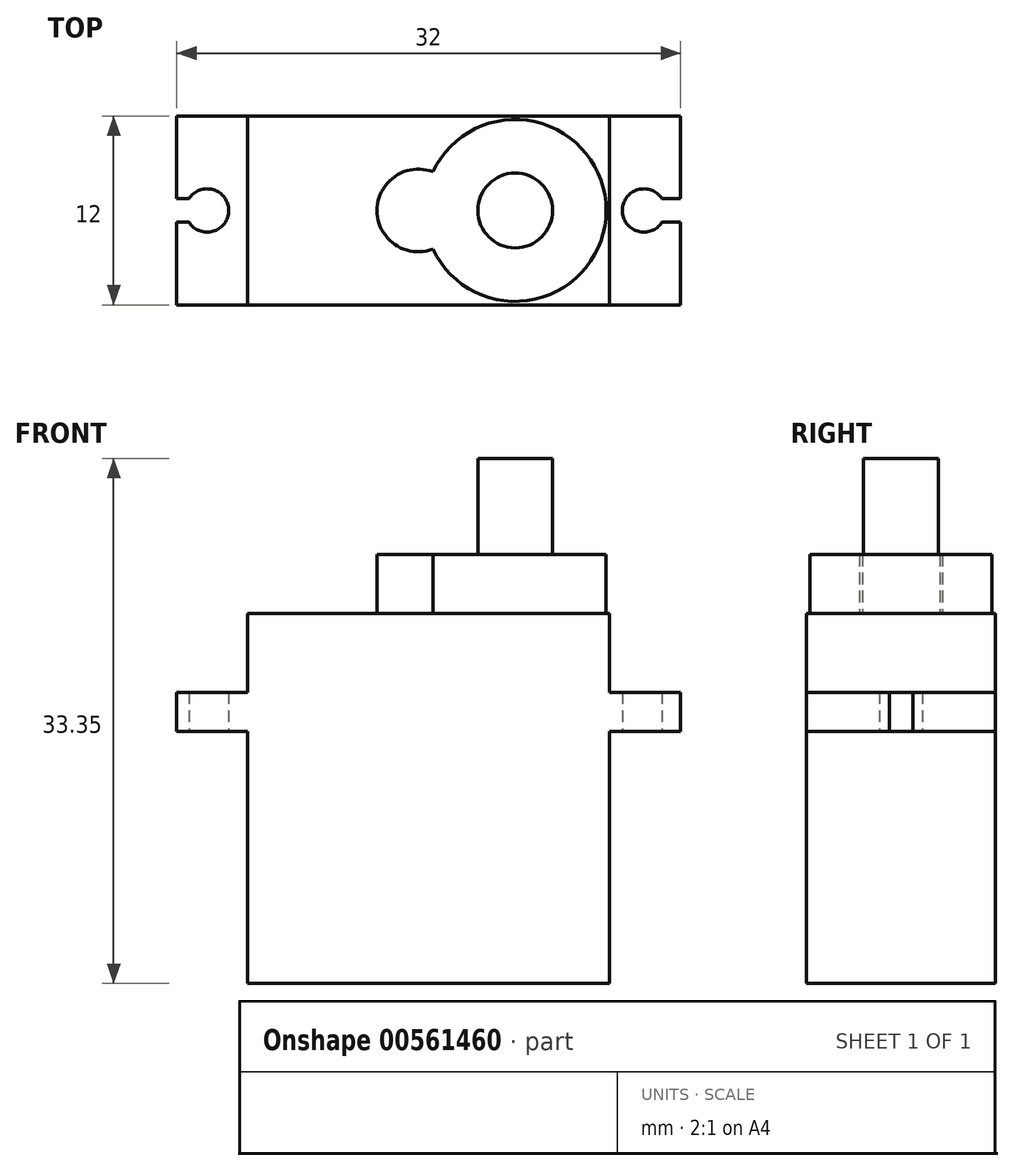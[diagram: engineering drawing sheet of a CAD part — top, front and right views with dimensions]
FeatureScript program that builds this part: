
annotation { "Feature Type Name" : "Feature", "Feature Type Description" : "" }
export const myFeature = defineFeature(function(context is Context, id is Id, definition is map)
    precondition{}
    {
        {
            var Q0;
            Q0=qCreatedBy(makeId("Top.planeOp"),FACE);
            var sketch = newSketch(context, id + "F0", { "sketchPlane" : qUnion([Q0])});
            skLineSegment(sketch, "E0.bottom", {"start": v(-11.3, 6) * mm, "end": v(11.7, 6) * mm});
            skLineSegment(sketch, "E0.top", {"start": v(-11.3, -6) * mm, "end": v(11.7, -6) * mm});
            skLineSegment(sketch, "E0.left", {"start": v(-11.3, 6) * mm, "end": v(-11.3, -6) * mm});
            skLineSegment(sketch, "E0.right", {"start": v(11.7, 6) * mm, "end": v(11.7, -6) * mm});
            skLineSegment(sketch, "E1.bottom", {"start": v(16.2, -6) * mm, "end": v(-15.8, -6) * mm});
            skLineSegment(sketch, "E1.top", {"start": v(16.2, 6) * mm, "end": v(-15.8, 6) * mm});
            skLineSegment(sketch, "E1.left", {"start": v(16.2, -6) * mm, "end": v(16.2, 6) * mm});
            skLineSegment(sketch, "E1.right", {"start": v(-15.8, -6) * mm, "end": v(-15.8, 6) * mm});
            skCircle(sketch, "E2", {"center": v(13.88, 0) * mm, "radius": 1.38 * mm});
            skPoint(sketch, "E2.centerSnap0", {"position": v(11.7, 0) * mm});
            skCircle(sketch, "E3", {"center": v(-13.88, 0) * mm, "radius": 1.38 * mm});
            skLineSegment(sketch, "E4.bottom", {"start": v(-29.2, 0.75) * mm, "end": v(30.8, 0.75) * mm});
            skLineSegment(sketch, "E4.top", {"start": v(-29.2, -0.75) * mm, "end": v(30.8, -0.75) * mm});
            skLineSegment(sketch, "E4.left", {"start": v(-29.2, 0.75) * mm, "end": v(-29.2, -0.75) * mm});
            skLineSegment(sketch, "E4.right", {"start": v(30.8, 0.75) * mm, "end": v(30.8, -0.75) * mm});
            skCircle(sketch, "E5", {"center": v(5.7, 0) * mm, "radius": 5.78 * mm});
            skCircle(sketch, "E6", {"center": v(-0.45, 0) * mm, "radius": 2.62 * mm});
            skSolve(sketch);
        }
        {
            var Q0;
            {var subQ0=sQuery(id+"F0.wireOp",EDGE,"E1.top");var subQ1=sQuery(id+"F0.wireOp",EDGE,"E0.left");var subQ2=makeQuery(id+"F0.imprint","INTERSECT",VERTEX,{"derivedFrom":[subQ1,subQ0]});Q0=makeQuery(id+"F0.imprint","IMPRINT",FACE,{"disambiguationData":[TD([[makeQuery(id+"F0.imprint","IMPRINT",EDGE,{"disambiguationData":[TD([[subQ2,-1.0]])],"derivedFrom":subQ1}),1.0]])]});}
            var Q1;
            {var subQ0=sQuery(id+"F0.wireOp",EDGE,"E1.bottom");var subQ1=sQuery(id+"F0.wireOp",EDGE,"E0.left");var subQ2=makeQuery(id+"F0.imprint","INTERSECT",VERTEX,{"derivedFrom":[subQ1,subQ0]});Q1=makeQuery(id+"F0.imprint","IMPRINT",FACE,{"disambiguationData":[TD([[makeQuery(id+"F0.imprint","IMPRINT",EDGE,{"disambiguationData":[TD([[subQ2,1.0]])],"derivedFrom":subQ1}),1.0]])]});}
            var Q2;
            {var subQ0=sQuery(id+"F0.wireOp",EDGE,"E4.bottom");var subQ1=sQuery(id+"F0.wireOp",EDGE,"E0.left");var subQ2=makeQuery(id+"F0.imprint","INTERSECT",VERTEX,{"derivedFrom":[subQ1,subQ0]});Q2=makeQuery(id+"F0.imprint","IMPRINT",FACE,{"disambiguationData":[TD([[makeQuery(id+"F0.imprint","IMPRINT",EDGE,{"disambiguationData":[TD([[subQ2,-1.0]])],"derivedFrom":subQ1}),1.0]])]});}
            var Q3;
            {var subQ0=sQuery(id+"F0.wireOp",EDGE,"E4.bottom");var subQ1=sQuery(id+"F0.wireOp",EDGE,"E0.left");var subQ2=makeQuery(id+"F0.imprint","INTERSECT",VERTEX,{"derivedFrom":[subQ1,subQ0]});Q3=makeQuery(id+"F0.imprint","IMPRINT",FACE,{"disambiguationData":[TD([[makeQuery(id+"F0.imprint","IMPRINT",EDGE,{"disambiguationData":[TD([[subQ2,-1.0]])],"derivedFrom":subQ1}),-1.0]])]});}
            var Q4;
            {var subQ4=sQuery(id+"F0.wireOp",EDGE,"E1.top");var subQ5=sQuery(id+"F0.wireOp",EDGE,"E0.left");var subQ6=makeQuery(id+"F0.imprint","INTERSECT",VERTEX,{"derivedFrom":[subQ5,subQ4]});Q4=makeQuery(id+"F0.imprint","IMPRINT",FACE,{"disambiguationData":[TD([[makeQuery(id+"F0.imprint","IMPRINT",EDGE,{"disambiguationData":[TD([[subQ6,-1.0]])],"derivedFrom":subQ5}),-1.0]])]});}
            var Q5;
            {var subQ4=sQuery(id+"F0.wireOp",EDGE,"E1.bottom");var subQ5=sQuery(id+"F0.wireOp",EDGE,"E0.left");var subQ6=makeQuery(id+"F0.imprint","INTERSECT",VERTEX,{"derivedFrom":[subQ5,subQ4]});Q5=makeQuery(id+"F0.imprint","IMPRINT",FACE,{"disambiguationData":[TD([[makeQuery(id+"F0.imprint","IMPRINT",EDGE,{"disambiguationData":[TD([[subQ6,1.0]])],"derivedFrom":subQ5}),-1.0]])]});}
            var Q6;
            {var subQ1=sQuery(id+"F0.wireOp",EDGE,"E1.top");var subQ5=sQuery(id+"F0.wireOp",EDGE,"E0.right");var subQ6=makeQuery(id+"F0.imprint","INTERSECT",VERTEX,{"derivedFrom":[subQ5,subQ1]});Q6=makeQuery(id+"F0.imprint","IMPRINT",FACE,{"disambiguationData":[TD([[makeQuery(id+"F0.imprint","IMPRINT",EDGE,{"disambiguationData":[TD([[subQ6,-1.0]])],"derivedFrom":subQ5}),1.0]])]});}
            var Q7;
            {var subQ1=sQuery(id+"F0.wireOp",EDGE,"E1.bottom");var subQ5=sQuery(id+"F0.wireOp",EDGE,"E0.right");var subQ6=makeQuery(id+"F0.imprint","INTERSECT",VERTEX,{"derivedFrom":[subQ5,subQ1]});Q7=makeQuery(id+"F0.imprint","IMPRINT",FACE,{"disambiguationData":[TD([[makeQuery(id+"F0.imprint","IMPRINT",EDGE,{"disambiguationData":[TD([[subQ6,1.0]])],"derivedFrom":subQ5}),1.0]])]});}
            var Q8;
            {var subQ0=sQuery(id+"F0.wireOp",EDGE,"E4.bottom");var subQ1=sQuery(id+"F0.wireOp",EDGE,"E0.right");var subQ2=makeQuery(id+"F0.imprint","INTERSECT",VERTEX,{"derivedFrom":[subQ1,subQ0]});Q8=makeQuery(id+"F0.imprint","IMPRINT",FACE,{"disambiguationData":[TD([[makeQuery(id+"F0.imprint","IMPRINT",EDGE,{"disambiguationData":[TD([[subQ2,-1.0]])],"derivedFrom":subQ1}),1.0]])]});}
            var Q9;
            {var subQ0=sQuery(id+"F0.wireOp",EDGE,"E6");var subQ1=sQuery(id+"F0.wireOp",EDGE,"E4.bottom");var subQ2=makeQuery(id+"F0.imprint","INTERSECT",VERTEX,{"disambiguationData":[OD(1.0)],"derivedFrom":[subQ1,subQ0]});Q9=makeQuery(id+"F0.imprint","IMPRINT",FACE,{"disambiguationData":[TD([[makeQuery(id+"F0.imprint","IMPRINT",EDGE,{"disambiguationData":[TD([[subQ2,-1.0]])],"derivedFrom":subQ1}),1.0]])]});}
            var Q10;
            {var subQ0=sQuery(id+"F0.wireOp",EDGE,"E6");var subQ1=sQuery(id+"F0.wireOp",EDGE,"E4.bottom");var subQ2=makeQuery(id+"F0.imprint","INTERSECT",VERTEX,{"disambiguationData":[OD(0.0)],"derivedFrom":[subQ1,subQ0]});Q10=makeQuery(id+"F0.imprint","IMPRINT",FACE,{"disambiguationData":[TD([[makeQuery(id+"F0.imprint","IMPRINT",EDGE,{"disambiguationData":[TD([[subQ2,-1.0]])],"derivedFrom":subQ1}),1.0]])]});}
            var Q11;
            {var subQ0=sQuery(id+"F0.wireOp",EDGE,"E6");var subQ1=sQuery(id+"F0.wireOp",EDGE,"E4.bottom");var subQ2=makeQuery(id+"F0.imprint","INTERSECT",VERTEX,{"disambiguationData":[OD(0.0)],"derivedFrom":[subQ1,subQ0]});Q11=makeQuery(id+"F0.imprint","IMPRINT",FACE,{"disambiguationData":[TD([[makeQuery(id+"F0.imprint","IMPRINT",EDGE,{"disambiguationData":[TD([[subQ2,-1.0]])],"derivedFrom":subQ1}),-1.0]])]});}
            var Q12;
            {var subQ0=sQuery(id+"F0.wireOp",EDGE,"E6");var subQ1=sQuery(id+"F0.wireOp",EDGE,"E4.top");var subQ2=makeQuery(id+"F0.imprint","INTERSECT",VERTEX,{"disambiguationData":[OD(0.0)],"derivedFrom":[subQ1,subQ0]});Q12=makeQuery(id+"F0.imprint","IMPRINT",FACE,{"disambiguationData":[TD([[makeQuery(id+"F0.imprint","IMPRINT",EDGE,{"disambiguationData":[TD([[subQ2,-1.0]])],"derivedFrom":subQ1}),-1.0]])]});}
            var Q13;
            {var subQ0=sQuery(id+"F0.wireOp",EDGE,"E5");var subQ1=sQuery(id+"F0.wireOp",EDGE,"E4.top");var subQ2=makeQuery(id+"F0.imprint","INTERSECT",VERTEX,{"disambiguationData":[OD(0.0)],"derivedFrom":[subQ1,subQ0]});Q13=makeQuery(id+"F0.imprint","IMPRINT",FACE,{"disambiguationData":[TD([[makeQuery(id+"F0.imprint","IMPRINT",EDGE,{"disambiguationData":[TD([[subQ2,-1.0]])],"derivedFrom":subQ1}),-1.0]])]});}
            var Q14;
            {var subQ0=sQuery(id+"F0.wireOp",EDGE,"E5");var subQ1=sQuery(id+"F0.wireOp",EDGE,"E4.bottom");var subQ2=makeQuery(id+"F0.imprint","INTERSECT",VERTEX,{"disambiguationData":[OD(0.0)],"derivedFrom":[subQ1,subQ0]});Q14=makeQuery(id+"F0.imprint","IMPRINT",FACE,{"disambiguationData":[TD([[makeQuery(id+"F0.imprint","IMPRINT",EDGE,{"disambiguationData":[TD([[subQ2,-1.0]])],"derivedFrom":subQ1}),-1.0]])]});}
            var Q15;
            {var subQ0=sQuery(id+"F0.wireOp",EDGE,"E5");var subQ1=sQuery(id+"F0.wireOp",EDGE,"E4.bottom");var subQ2=makeQuery(id+"F0.imprint","INTERSECT",VERTEX,{"disambiguationData":[OD(0.0)],"derivedFrom":[subQ1,subQ0]});Q15=makeQuery(id+"F0.imprint","IMPRINT",FACE,{"disambiguationData":[TD([[makeQuery(id+"F0.imprint","IMPRINT",EDGE,{"disambiguationData":[TD([[subQ2,-1.0]])],"derivedFrom":subQ1}),1.0]])]});}
            var Q16;
            {var subQ0=sQuery(id+"F0.wireOp",EDGE,"E6");var subQ1=sQuery(id+"F0.wireOp",EDGE,"E4.bottom");var subQ2=makeQuery(id+"F0.imprint","INTERSECT",VERTEX,{"disambiguationData":[OD(1.0)],"derivedFrom":[subQ1,subQ0]});Q16=makeQuery(id+"F0.imprint","IMPRINT",FACE,{"disambiguationData":[TD([[makeQuery(id+"F0.imprint","IMPRINT",EDGE,{"disambiguationData":[TD([[subQ2,-1.0]])],"derivedFrom":subQ1}),-1.0]])]});}
            var Q17;
            {var subQ0=sQuery(id+"F0.wireOp",EDGE,"E6");var subQ1=sQuery(id+"F0.wireOp",EDGE,"E4.top");var subQ2=makeQuery(id+"F0.imprint","INTERSECT",VERTEX,{"disambiguationData":[OD(1.0)],"derivedFrom":[subQ1,subQ0]});Q17=makeQuery(id+"F0.imprint","IMPRINT",FACE,{"disambiguationData":[TD([[makeQuery(id+"F0.imprint","IMPRINT",EDGE,{"disambiguationData":[TD([[subQ2,-1.0]])],"derivedFrom":subQ1}),-1.0]])]});}
            var Q18;
            {var subQ0=sQuery(id+"F0.wireOp",EDGE,"E4.bottom");var subQ1=sQuery(id+"F0.wireOp",EDGE,"E0.right");var subQ2=makeQuery(id+"F0.imprint","INTERSECT",VERTEX,{"derivedFrom":[subQ1,subQ0]});Q18=makeQuery(id+"F0.imprint","IMPRINT",FACE,{"disambiguationData":[TD([[makeQuery(id+"F0.imprint","IMPRINT",EDGE,{"disambiguationData":[TD([[subQ2,-1.0]])],"derivedFrom":subQ1}),-1.0]])]});}
            extrude(context, id + "F1", {"entities" : qUnion([Q0, Q1, Q2, Q3, Q4, Q5, Q6, Q7, Q8, Q9, Q10, Q11, Q12, Q13, Q14, Q15, Q16, Q17, Q18]), "depth" : 2.5 * mm, "offsetDistance" : 25 * mm});
        }
        {
            var Q0;
            {var subQ0=sQuery(id+"F0.wireOp",EDGE,"E6");var subQ1=sQuery(id+"F0.wireOp",EDGE,"E4.bottom");var subQ2=makeQuery(id+"F0.imprint","INTERSECT",VERTEX,{"disambiguationData":[OD(1.0)],"derivedFrom":[subQ1,subQ0]});Q0=makeQuery(id+"F0.imprint","IMPRINT",FACE,{"disambiguationData":[TD([[makeQuery(id+"F0.imprint","IMPRINT",EDGE,{"disambiguationData":[TD([[subQ2,-1.0]])],"derivedFrom":subQ1}),1.0]])]});}
            var Q1;
            {var subQ0=sQuery(id+"F0.wireOp",EDGE,"E6");var subQ1=sQuery(id+"F0.wireOp",EDGE,"E4.top");var subQ2=makeQuery(id+"F0.imprint","INTERSECT",VERTEX,{"disambiguationData":[OD(1.0)],"derivedFrom":[subQ1,subQ0]});Q1=makeQuery(id+"F0.imprint","IMPRINT",FACE,{"disambiguationData":[TD([[makeQuery(id+"F0.imprint","IMPRINT",EDGE,{"disambiguationData":[TD([[subQ2,-1.0]])],"derivedFrom":subQ1}),-1.0]])]});}
            var Q2;
            {var subQ0=sQuery(id+"F0.wireOp",EDGE,"E6");var subQ1=sQuery(id+"F0.wireOp",EDGE,"E4.bottom");var subQ2=makeQuery(id+"F0.imprint","INTERSECT",VERTEX,{"disambiguationData":[OD(1.0)],"derivedFrom":[subQ1,subQ0]});Q2=makeQuery(id+"F0.imprint","IMPRINT",FACE,{"disambiguationData":[TD([[makeQuery(id+"F0.imprint","IMPRINT",EDGE,{"disambiguationData":[TD([[subQ2,-1.0]])],"derivedFrom":subQ1}),-1.0]])]});}
            var Q3;
            {var subQ0=sQuery(id+"F0.wireOp",EDGE,"E5");var subQ1=sQuery(id+"F0.wireOp",EDGE,"E4.bottom");var subQ2=makeQuery(id+"F0.imprint","INTERSECT",VERTEX,{"disambiguationData":[OD(0.0)],"derivedFrom":[subQ1,subQ0]});Q3=makeQuery(id+"F0.imprint","IMPRINT",FACE,{"disambiguationData":[TD([[makeQuery(id+"F0.imprint","IMPRINT",EDGE,{"disambiguationData":[TD([[subQ2,-1.0]])],"derivedFrom":subQ1}),-1.0]])]});}
            var Q4;
            {var subQ0=sQuery(id+"F0.wireOp",EDGE,"E5");var subQ1=sQuery(id+"F0.wireOp",EDGE,"E4.bottom");var subQ2=makeQuery(id+"F0.imprint","INTERSECT",VERTEX,{"disambiguationData":[OD(0.0)],"derivedFrom":[subQ1,subQ0]});Q4=makeQuery(id+"F0.imprint","IMPRINT",FACE,{"disambiguationData":[TD([[makeQuery(id+"F0.imprint","IMPRINT",EDGE,{"disambiguationData":[TD([[subQ2,-1.0]])],"derivedFrom":subQ1}),1.0]])]});}
            var Q5;
            {var subQ0=sQuery(id+"F0.wireOp",EDGE,"E6");var subQ1=sQuery(id+"F0.wireOp",EDGE,"E4.bottom");var subQ2=makeQuery(id+"F0.imprint","INTERSECT",VERTEX,{"disambiguationData":[OD(0.0)],"derivedFrom":[subQ1,subQ0]});Q5=makeQuery(id+"F0.imprint","IMPRINT",FACE,{"disambiguationData":[TD([[makeQuery(id+"F0.imprint","IMPRINT",EDGE,{"disambiguationData":[TD([[subQ2,-1.0]])],"derivedFrom":subQ1}),1.0]])]});}
            var Q6;
            {var subQ0=sQuery(id+"F0.wireOp",EDGE,"E6");var subQ1=sQuery(id+"F0.wireOp",EDGE,"E4.bottom");var subQ2=makeQuery(id+"F0.imprint","INTERSECT",VERTEX,{"disambiguationData":[OD(0.0)],"derivedFrom":[subQ1,subQ0]});Q6=makeQuery(id+"F0.imprint","IMPRINT",FACE,{"disambiguationData":[TD([[makeQuery(id+"F0.imprint","IMPRINT",EDGE,{"disambiguationData":[TD([[subQ2,-1.0]])],"derivedFrom":subQ1}),-1.0]])]});}
            var Q7;
            {var subQ0=sQuery(id+"F0.wireOp",EDGE,"E6");var subQ1=sQuery(id+"F0.wireOp",EDGE,"E4.top");var subQ2=makeQuery(id+"F0.imprint","INTERSECT",VERTEX,{"disambiguationData":[OD(0.0)],"derivedFrom":[subQ1,subQ0]});Q7=makeQuery(id+"F0.imprint","IMPRINT",FACE,{"disambiguationData":[TD([[makeQuery(id+"F0.imprint","IMPRINT",EDGE,{"disambiguationData":[TD([[subQ2,-1.0]])],"derivedFrom":subQ1}),-1.0]])]});}
            var Q8;
            {var subQ0=sQuery(id+"F0.wireOp",EDGE,"E5");var subQ1=sQuery(id+"F0.wireOp",EDGE,"E4.top");var subQ2=makeQuery(id+"F0.imprint","INTERSECT",VERTEX,{"disambiguationData":[OD(0.0)],"derivedFrom":[subQ1,subQ0]});Q8=makeQuery(id+"F0.imprint","IMPRINT",FACE,{"disambiguationData":[TD([[makeQuery(id+"F0.imprint","IMPRINT",EDGE,{"disambiguationData":[TD([[subQ2,-1.0]])],"derivedFrom":subQ1}),-1.0]])]});}
            extrude(context, id + "F2", {"entities" : qUnion([Q0, Q1, Q2, Q3, Q4, Q5, Q6, Q7, Q8]), "operationType" : NewBodyOperationType.ADD, "depth" : 11.25 * mm, "offsetDistance" : 25 * mm});
        }
        {
            var Q0;
            {var subQ0=sQuery(id+"F0.wireOp",EDGE,"E1.top");var subQ5=sQuery(id+"F0.wireOp",EDGE,"E0.left");var subQ9=makeQuery(id+"F0.imprint","INTERSECT",VERTEX,{"derivedFrom":[subQ5,subQ0]});Q0=makeQuery(id+"F0.imprint","IMPRINT",FACE,{"disambiguationData":[TD([[makeQuery(id+"F0.imprint","IMPRINT",EDGE,{"disambiguationData":[TD([[subQ9,-1.0]])],"derivedFrom":subQ5}),1.0]])]});}
            var Q1;
            {var subQ1=sQuery(id+"F0.wireOp",EDGE,"E0.left");var subQ5=sQuery(id+"F0.wireOp",EDGE,"E1.bottom");var subQ9=makeQuery(id+"F0.imprint","INTERSECT",VERTEX,{"derivedFrom":[subQ1,subQ5]});Q1=makeQuery(id+"F0.imprint","IMPRINT",FACE,{"disambiguationData":[TD([[makeQuery(id+"F0.imprint","IMPRINT",EDGE,{"disambiguationData":[TD([[subQ9,1.0]])],"derivedFrom":subQ1}),1.0]])]});}
            var Q2;
            {var subQ0=sQuery(id+"F0.wireOp",EDGE,"E4.bottom");var subQ1=sQuery(id+"F0.wireOp",EDGE,"E0.left");var subQ2=makeQuery(id+"F0.imprint","INTERSECT",VERTEX,{"derivedFrom":[subQ1,subQ0]});Q2=makeQuery(id+"F0.imprint","IMPRINT",FACE,{"disambiguationData":[TD([[makeQuery(id+"F0.imprint","IMPRINT",EDGE,{"disambiguationData":[TD([[subQ2,-1.0]])],"derivedFrom":subQ1}),1.0]])]});}
            var Q3;
            {var subQ0=sQuery(id+"F0.wireOp",EDGE,"E6");var subQ1=sQuery(id+"F0.wireOp",EDGE,"E4.bottom");var subQ2=makeQuery(id+"F0.imprint","INTERSECT",VERTEX,{"disambiguationData":[OD(0.0)],"derivedFrom":[subQ1,subQ0]});Q3=makeQuery(id+"F0.imprint","IMPRINT",FACE,{"disambiguationData":[TD([[makeQuery(id+"F0.imprint","IMPRINT",EDGE,{"disambiguationData":[TD([[subQ2,-1.0]])],"derivedFrom":subQ1}),-1.0]])]});}
            var Q4;
            {var subQ0=sQuery(id+"F0.wireOp",EDGE,"E6");var subQ1=sQuery(id+"F0.wireOp",EDGE,"E4.bottom");var subQ2=makeQuery(id+"F0.imprint","INTERSECT",VERTEX,{"disambiguationData":[OD(0.0)],"derivedFrom":[subQ1,subQ0]});Q4=makeQuery(id+"F0.imprint","IMPRINT",FACE,{"disambiguationData":[TD([[makeQuery(id+"F0.imprint","IMPRINT",EDGE,{"disambiguationData":[TD([[subQ2,-1.0]])],"derivedFrom":subQ1}),1.0]])]});}
            var Q5;
            {var subQ0=sQuery(id+"F0.wireOp",EDGE,"E6");var subQ1=sQuery(id+"F0.wireOp",EDGE,"E4.top");var subQ2=makeQuery(id+"F0.imprint","INTERSECT",VERTEX,{"disambiguationData":[OD(0.0)],"derivedFrom":[subQ1,subQ0]});Q5=makeQuery(id+"F0.imprint","IMPRINT",FACE,{"disambiguationData":[TD([[makeQuery(id+"F0.imprint","IMPRINT",EDGE,{"disambiguationData":[TD([[subQ2,-1.0]])],"derivedFrom":subQ1}),-1.0]])]});}
            var Q6;
            {var subQ0=sQuery(id+"F0.wireOp",EDGE,"E5");var subQ1=sQuery(id+"F0.wireOp",EDGE,"E4.top");var subQ2=makeQuery(id+"F0.imprint","INTERSECT",VERTEX,{"disambiguationData":[OD(0.0)],"derivedFrom":[subQ1,subQ0]});Q6=makeQuery(id+"F0.imprint","IMPRINT",FACE,{"disambiguationData":[TD([[makeQuery(id+"F0.imprint","IMPRINT",EDGE,{"disambiguationData":[TD([[subQ2,-1.0]])],"derivedFrom":subQ1}),-1.0]])]});}
            var Q7;
            {var subQ0=sQuery(id+"F0.wireOp",EDGE,"E5");var subQ1=sQuery(id+"F0.wireOp",EDGE,"E4.bottom");var subQ2=makeQuery(id+"F0.imprint","INTERSECT",VERTEX,{"disambiguationData":[OD(0.0)],"derivedFrom":[subQ1,subQ0]});Q7=makeQuery(id+"F0.imprint","IMPRINT",FACE,{"disambiguationData":[TD([[makeQuery(id+"F0.imprint","IMPRINT",EDGE,{"disambiguationData":[TD([[subQ2,-1.0]])],"derivedFrom":subQ1}),-1.0]])]});}
            var Q8;
            {var subQ0=sQuery(id+"F0.wireOp",EDGE,"E5");var subQ1=sQuery(id+"F0.wireOp",EDGE,"E4.bottom");var subQ2=makeQuery(id+"F0.imprint","INTERSECT",VERTEX,{"disambiguationData":[OD(0.0)],"derivedFrom":[subQ1,subQ0]});Q8=makeQuery(id+"F0.imprint","IMPRINT",FACE,{"disambiguationData":[TD([[makeQuery(id+"F0.imprint","IMPRINT",EDGE,{"disambiguationData":[TD([[subQ2,-1.0]])],"derivedFrom":subQ1}),1.0]])]});}
            var Q9;
            {var subQ0=sQuery(id+"F0.wireOp",EDGE,"E6");var subQ1=sQuery(id+"F0.wireOp",EDGE,"E4.bottom");var subQ2=makeQuery(id+"F0.imprint","INTERSECT",VERTEX,{"disambiguationData":[OD(1.0)],"derivedFrom":[subQ1,subQ0]});Q9=makeQuery(id+"F0.imprint","IMPRINT",FACE,{"disambiguationData":[TD([[makeQuery(id+"F0.imprint","IMPRINT",EDGE,{"disambiguationData":[TD([[subQ2,-1.0]])],"derivedFrom":subQ1}),1.0]])]});}
            var Q10;
            {var subQ0=sQuery(id+"F0.wireOp",EDGE,"E6");var subQ1=sQuery(id+"F0.wireOp",EDGE,"E4.top");var subQ2=makeQuery(id+"F0.imprint","INTERSECT",VERTEX,{"disambiguationData":[OD(1.0)],"derivedFrom":[subQ1,subQ0]});Q10=makeQuery(id+"F0.imprint","IMPRINT",FACE,{"disambiguationData":[TD([[makeQuery(id+"F0.imprint","IMPRINT",EDGE,{"disambiguationData":[TD([[subQ2,-1.0]])],"derivedFrom":subQ1}),-1.0]])]});}
            var Q11;
            {var subQ0=sQuery(id+"F0.wireOp",EDGE,"E6");var subQ1=sQuery(id+"F0.wireOp",EDGE,"E4.bottom");var subQ2=makeQuery(id+"F0.imprint","INTERSECT",VERTEX,{"disambiguationData":[OD(1.0)],"derivedFrom":[subQ1,subQ0]});Q11=makeQuery(id+"F0.imprint","IMPRINT",FACE,{"disambiguationData":[TD([[makeQuery(id+"F0.imprint","IMPRINT",EDGE,{"disambiguationData":[TD([[subQ2,-1.0]])],"derivedFrom":subQ1}),-1.0]])]});}
            var Q12;
            {var subQ0=sQuery(id+"F0.wireOp",EDGE,"E4.bottom");var subQ1=sQuery(id+"F0.wireOp",EDGE,"E0.right");var subQ2=makeQuery(id+"F0.imprint","INTERSECT",VERTEX,{"derivedFrom":[subQ1,subQ0]});Q12=makeQuery(id+"F0.imprint","IMPRINT",FACE,{"disambiguationData":[TD([[makeQuery(id+"F0.imprint","IMPRINT",EDGE,{"disambiguationData":[TD([[subQ2,-1.0]])],"derivedFrom":subQ1}),-1.0]])]});}
            extrude(context, id + "F3", {"entities" : qUnion([Q0, Q1, Q2, Q3, Q4, Q5, Q6, Q7, Q8, Q9, Q10, Q11, Q12]), "operationType" : NewBodyOperationType.ADD, "depth" : 7.5 * mm, "offsetDistance" : 25 * mm, "hasSecondDirection" : true, "secondDirectionOppositeDirection" : true, "secondDirectionDepth" : 16 * mm});
        }
        {
            var Q0;
            Q0=makeQuery(id+"F2.opExtrude","CAP_FACE",FACE,{"disambiguationData":[OSD([sQuery(id+"F0.wireOp",EDGE,"E5"),sQuery(id+"F0.wireOp",EDGE,"E6")])],"isStart":false});
            var sketch = newSketch(context, id + "F4", { "sketchPlane" : qUnion([Q0])});
            skCircle(sketch, "E7", {"center": v(5.7, 0) * mm, "radius": 2.38 * mm});
            skSolve(sketch);
        }
        {
            var Q0;
            Q0=makeQuery(id+"F4.imprint","IMPRINT",FACE,{"disambiguationData":[TD([[makeQuery(id+"F4.imprint","IMPRINT",EDGE,{"derivedFrom":sQuery(id+"F4.wireOp",EDGE,"E7")}),1.0]])]});
            extrude(context, id + "F5", {"entities" : qUnion([Q0]), "operationType" : NewBodyOperationType.ADD, "depth" : 6.1 * mm, "offsetDistance" : 25 * mm});
        }
    });
